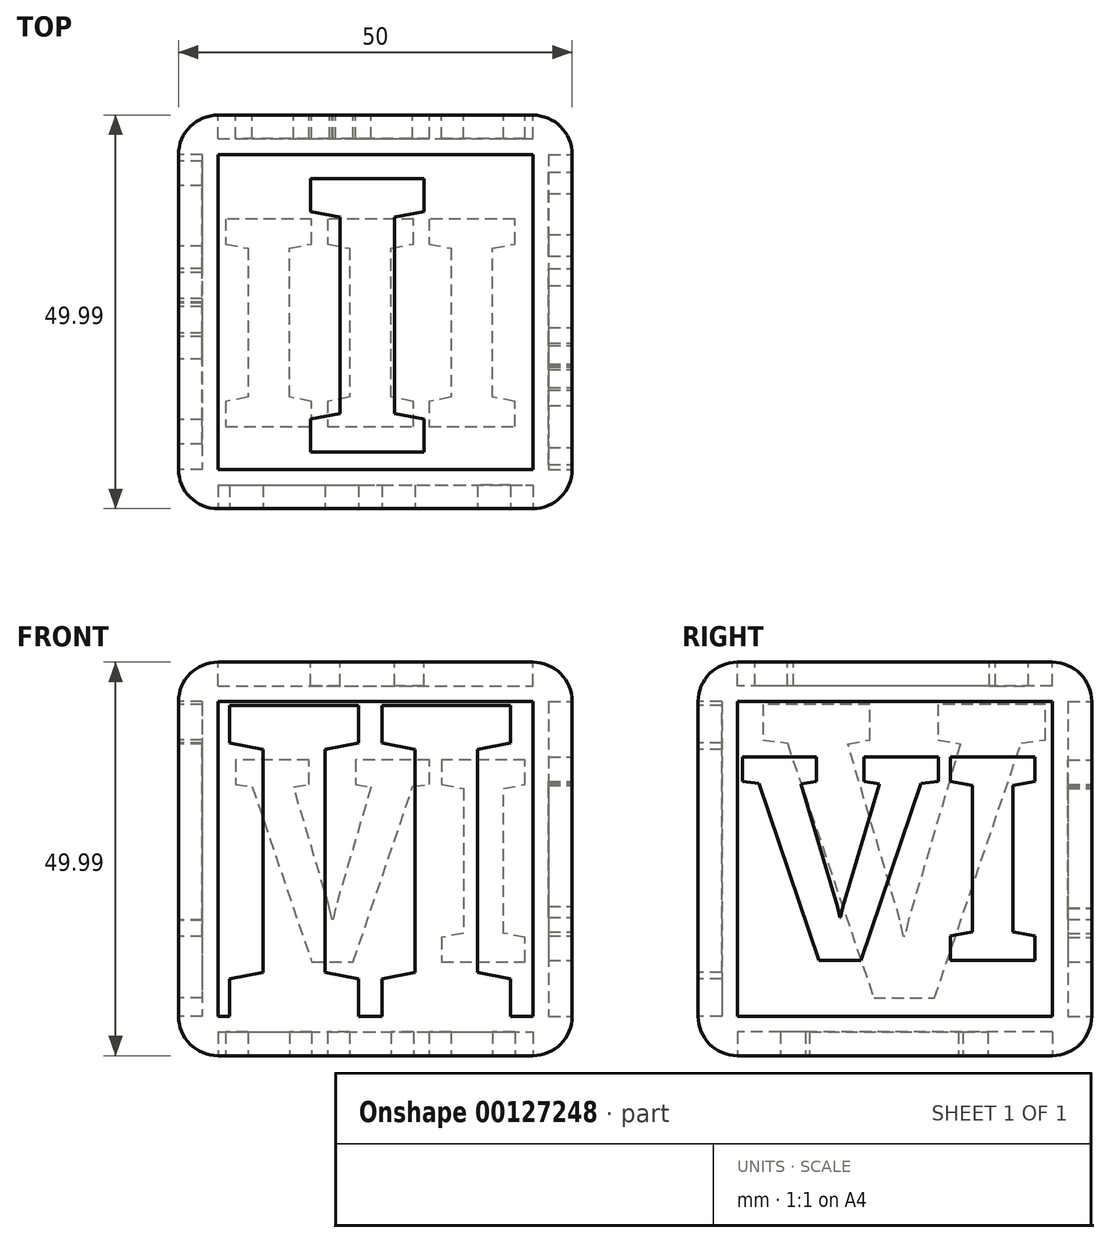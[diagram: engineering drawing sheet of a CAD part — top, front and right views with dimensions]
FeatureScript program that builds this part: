
annotation { "Feature Type Name" : "Feature", "Feature Type Description" : "" }
export const myFeature = defineFeature(function(context is Context, id is Id, definition is map)
    precondition{}
    {
        {
            var Q0;
            Q0=qCreatedBy(makeId("Top.planeOp"),FACE);
            var sketch = newSketch(context, id + "F0", { "sketchPlane" : qUnion([Q0])});
            skLineSegment(sketch, "E0.bottom", {"start": v(-22.33, 23.42) * mm, "end": v(27.67, 23.42) * mm});
            skLineSegment(sketch, "E0.top", {"start": v(-22.33, -26.57) * mm, "end": v(27.67, -26.57) * mm});
            skLineSegment(sketch, "E0.left", {"start": v(-22.33, 23.42) * mm, "end": v(-22.33, -26.57) * mm});
            skLineSegment(sketch, "E0.right", {"start": v(27.67, 23.42) * mm, "end": v(27.67, -26.57) * mm});
            skSolve(sketch);
        }
        {
            var Q0;
            Q0=makeQuery(id+"F0.imprint","IMPRINT",FACE,{"disambiguationData":[TD([[makeQuery(id+"F0.imprint","IMPRINT",EDGE,{"derivedFrom":sQuery(id+"F0.wireOp",EDGE,"E0.bottom")}),-1.0]])]});
            extrude(context, id + "F1", {"entities" : qUnion([Q0]), "depth" : 50 * mm});
        }
        {
            var Q0;
            Q0=makeQuery(id+"F1.opExtrude","CAP_EDGE",EDGE,{"disambiguationData":[OSD([sQuery(id+"F0.wireOp",EDGE,"E0.top")])],"isStart":false});
            var Q1;
            Q1=makeQuery(id+"F1.opExtrude","CAP_EDGE",EDGE,{"disambiguationData":[OSD([sQuery(id+"F0.wireOp",EDGE,"E0.right")])],"isStart":false});
            var Q2;
            Q2=makeQuery(id+"F1.opExtrude","SWEPT_EDGE",EDGE,{"disambiguationData":[OSD([sQuery(id+"F0.wireOp",EDGE,"E0.top"),sQuery(id+"F0.wireOp",EDGE,"E0.right")])]});
            var Q3;
            Q3=makeQuery(id+"F1.opExtrude","CAP_EDGE",EDGE,{"disambiguationData":[OSD([sQuery(id+"F0.wireOp",EDGE,"E0.left")])],"isStart":false});
            var Q4;
            Q4=makeQuery(id+"F1.opExtrude","SWEPT_EDGE",EDGE,{"disambiguationData":[OSD([sQuery(id+"F0.wireOp",EDGE,"E0.top"),sQuery(id+"F0.wireOp",EDGE,"E0.left")])]});
            var Q5;
            Q5=makeQuery(id+"F1.opExtrude","CAP_EDGE",EDGE,{"disambiguationData":[OSD([sQuery(id+"F0.wireOp",EDGE,"E0.bottom")])],"isStart":false});
            var Q6;
            Q6=makeQuery(id+"F1.opExtrude","SWEPT_EDGE",EDGE,{"disambiguationData":[OSD([sQuery(id+"F0.wireOp",EDGE,"E0.bottom"),sQuery(id+"F0.wireOp",EDGE,"E0.left")])]});
            var Q7;
            Q7=makeQuery(id+"F1.opExtrude","SWEPT_EDGE",EDGE,{"disambiguationData":[OSD([sQuery(id+"F0.wireOp",EDGE,"E0.bottom"),sQuery(id+"F0.wireOp",EDGE,"E0.right")])]});
            var Q8;
            Q8=makeQuery(id+"F1.opExtrude","CAP_EDGE",EDGE,{"disambiguationData":[OSD([sQuery(id+"F0.wireOp",EDGE,"E0.bottom")])],"isStart":true});
            var Q9;
            Q9=makeQuery(id+"F1.opExtrude","CAP_EDGE",EDGE,{"disambiguationData":[OSD([sQuery(id+"F0.wireOp",EDGE,"E0.right")])],"isStart":true});
            var Q10;
            Q10=makeQuery(id+"F1.opExtrude","CAP_EDGE",EDGE,{"disambiguationData":[OSD([sQuery(id+"F0.wireOp",EDGE,"E0.top")])],"isStart":true});
            var Q11;
            Q11=makeQuery(id+"F1.opExtrude","CAP_EDGE",EDGE,{"disambiguationData":[OSD([sQuery(id+"F0.wireOp",EDGE,"E0.left")])],"isStart":true});
            fillet(context, id + "F2", {"entities" : qUnion([Q0, Q1, Q2, Q3, Q4, Q5, Q6, Q7, Q8, Q9, Q10, Q11]), "radius" : 5 * mm, "tangentPropagation" : true, "allowEdgeOverflow" : false});
        }
        {
            var Q0;
            Q0=makeQuery(id+"F1.opExtrude","CAP_FACE",FACE,{"disambiguationData":[OSD([sQuery(id+"F0.wireOp",EDGE,"E0.bottom"),sQuery(id+"F0.wireOp",EDGE,"E0.top"),sQuery(id+"F0.wireOp",EDGE,"E0.left"),sQuery(id+"F0.wireOp",EDGE,"E0.right")])],"isStart":false});
            var sketch = newSketch(context, id + "F3", { "sketchPlane" : qUnion([Q0])});
            skText(sketch, "E1", { "text": "I", "fontName": "RobotoSlab-Bold.ttf"});
            const initialGuessF3  = {"E1": [-0.00688, -0.01938, 1, 0, 0.03519]};
            skSetInitialGuess(sketch, initialGuessF3);
            skSolve(sketch);
        }
        {
            var Q0;
            Q0=makeQuery(id+"F1.opExtrude","SWEPT_FACE",FACE,{"disambiguationData":[OSD([sQuery(id+"F0.wireOp",EDGE,"E0.top")])]});
            var sketch = newSketch(context, id + "F4", { "sketchPlane" : qUnion([Q0])});
            skText(sketch, "E2", { "text": "II", "fontName": "RobotoSlab-Bold.ttf"});
            const initialGuessF4  = {"E2": [-0.01733, 0.005, 1, 0, 0.04]};
            skSetInitialGuess(sketch, initialGuessF4);
            skSolve(sketch);
        }
        {
            var Q0;
            Q0=makeQuery(id+"F1.opExtrude","CAP_FACE",FACE,{"disambiguationData":[OSD([sQuery(id+"F0.wireOp",EDGE,"E0.bottom"),sQuery(id+"F0.wireOp",EDGE,"E0.top"),sQuery(id+"F0.wireOp",EDGE,"E0.left"),sQuery(id+"F0.wireOp",EDGE,"E0.right")])],"isStart":true});
            var sketch = newSketch(context, id + "F5", { "sketchPlane" : qUnion([Q0])});
            skText(sketch, "E3", { "text": "III", "fontName": "RobotoSlab-Bold.ttf"});
            const initialGuessF5  = {"E3": [-0.01733, -0.01023, 1, 0, 0.0267]};
            skSetInitialGuess(sketch, initialGuessF5);
            skSolve(sketch);
        }
        {
            var Q0;
            Q0=makeQuery(id+"F1.opExtrude","SWEPT_FACE",FACE,{"disambiguationData":[OSD([sQuery(id+"F0.wireOp",EDGE,"E0.bottom")])]});
            var sketch = newSketch(context, id + "F6", { "sketchPlane" : qUnion([Q0])});
            skText(sketch, "E4", { "text": "IV", "fontName": "RobotoSlab-Bold.ttf"});
            const initialGuessF6  = {"E4": [-0.02267, 0.01194, 1, 0, 0.02594]};
            skSetInitialGuess(sketch, initialGuessF6);
            skSolve(sketch);
        }
        {
            var Q0;
            Q0=makeQuery(id+"F1.opExtrude","SWEPT_FACE",FACE,{"disambiguationData":[OSD([sQuery(id+"F0.wireOp",EDGE,"E0.left")])]});
            var sketch = newSketch(context, id + "F7", { "sketchPlane" : qUnion([Q0])});
            skText(sketch, "E5", { "text": "V", "fontName": "RobotoSlab-Bold.ttf"});
            const initialGuessF7  = {"E5": [-0.01842, 0.00731, 1, 0, 0.0378]};
            skSetInitialGuess(sketch, initialGuessF7);
            skSolve(sketch);
        }
        {
            var Q0;
            Q0=makeQuery(id+"F1.opExtrude","SWEPT_FACE",FACE,{"disambiguationData":[OSD([sQuery(id+"F0.wireOp",EDGE,"E0.right")])]});
            var sketch = newSketch(context, id + "F8", { "sketchPlane" : qUnion([Q0])});
            skText(sketch, "E6", { "text": "VI", "fontName": "RobotoSlab-Bold.ttf"});
            const initialGuessF8  = {"E6": [-0.02157, 0.0121, 1, 0, 0.0262]};
            skSetInitialGuess(sketch, initialGuessF8);
            skSolve(sketch);
        }
        {
            var Q0;
            Q0=makeQuery(id+"F3.imprint","IMPRINT",FACE,{"disambiguationData":[TD([[makeQuery(id+"F3.imprint","IMPRINT",EDGE,{"derivedFrom":sQuery(id+"F3.wireOp",EDGE,"E1.sketch_text.stroke-0")}),1.0]])]});
            extrude(context, id + "F9", {"entities" : qUnion([Q0]), "operationType" : NewBodyOperationType.REMOVE, "oppositeDirection" : true, "depth" : 3 * mm});
        }
        {
            var Q0;
            Q0=makeQuery(id+"F4.imprint","IMPRINT",FACE,{"disambiguationData":[TD([[makeQuery(id+"F4.imprint","IMPRINT",EDGE,{"derivedFrom":sQuery(id+"F4.wireOp",EDGE,"E2.sketch_text.stroke-0")}),1.0]])]});
            extrude(context, id + "F10", {"entities" : qUnion([Q0]), "operationType" : NewBodyOperationType.REMOVE, "oppositeDirection" : true, "depth" : 3 * mm});
        }
        {
            var Q0;
            Q0=makeQuery(id+"F8.imprint","IMPRINT",FACE,{"disambiguationData":[TD([[makeQuery(id+"F8.imprint","IMPRINT",EDGE,{"derivedFrom":sQuery(id+"F8.wireOp",EDGE,"E6.sketch_text.stroke-0")}),1.0]])]});
            extrude(context, id + "F11", {"entities" : qUnion([Q0]), "operationType" : NewBodyOperationType.REMOVE, "oppositeDirection" : true, "depth" : 3 * mm});
        }
        {
            var Q0;
            Q0=makeQuery(id+"F6.imprint","IMPRINT",FACE,{"disambiguationData":[TD([[makeQuery(id+"F6.imprint","IMPRINT",EDGE,{"derivedFrom":sQuery(id+"F6.wireOp",EDGE,"E4.sketch_text.stroke-0")}),1.0]])]});
            extrude(context, id + "F12", {"entities" : qUnion([Q0]), "operationType" : NewBodyOperationType.REMOVE, "oppositeDirection" : true, "depth" : 3 * mm});
        }
        {
            var Q0;
            Q0=makeQuery(id+"F7.imprint","IMPRINT",FACE,{"disambiguationData":[TD([[makeQuery(id+"F7.imprint","IMPRINT",EDGE,{"derivedFrom":sQuery(id+"F7.wireOp",EDGE,"E5.sketch_text.stroke-0")}),1.0]])]});
            extrude(context, id + "F13", {"entities" : qUnion([Q0]), "operationType" : NewBodyOperationType.REMOVE, "oppositeDirection" : true, "depth" : 3 * mm});
        }
        {
            var Q0;
            Q0=makeQuery(id+"F5.imprint","IMPRINT",FACE,{"disambiguationData":[TD([[makeQuery(id+"F5.imprint","IMPRINT",EDGE,{"derivedFrom":sQuery(id+"F5.wireOp",EDGE,"E3.sketch_text.stroke-0")}),1.0]])]});
            extrude(context, id + "F14", {"entities" : qUnion([Q0]), "operationType" : NewBodyOperationType.REMOVE, "oppositeDirection" : true, "depth" : 3 * mm});
        }
    });
